# Revit family: PRD_AR_WshBsnWsts_RONDAWasteValve_ZANMW0030_0031
name_source: partatom
category: Plumbing Fixtures
revit_build: Autodesk Revit 2018 (Build: 20190510_1515(x64)
units: mm (PartAtom-declared; Revit-internal decimal feet)

## family parameters
Always vertical = No
Cut with Voids When Loaded = No
OmniClass Number = 23.45.00.00
OmniClass Title = Sanitary, Laundry, and Cleaning Equipment
Part Type = Normal
Room Calculation Point = No
Round Connector Dimension = Use Diameter
Shared = Yes
Work Plane-Based = Yes

## types (2) — shared parameters
AssetType = Fixed
Category = Pr_70_55_96_97, Washbasin wastes
Default Elevation = 1219 mm
DurationUnit = year
Features = chrome-plated brass, shaft valve and dome
Finish = chromed
GrossWeight = 0.34 kg
IfcExportAs = IfcWasteTerminalType
IfcExportType = WASTETRAP
IntegralAccessories = incl. an adapter for retrofitting on click closing dome
Manufacturer = KWC Group AG
ManufacturerName = KWC Group AG
ManufacturerURL = www.kwc.com
Material = brass
NBSDescription = Wastes for wash basins
NBSReference = 45-35-70/372
NetWeight = 0.32 kg
NominalDepth = 63 mm
NominalWidth = 63 mm
OutletConnectionSize = 32 mm
ProductInformation = https://pim.kwc.com
Quantity = 1
QuantityUom = Piece
Size = DN 32 (1 1/4 inch.)
TailorMade = No
URL = www.kwc.com
Uniclass2015Code = Pr_70_55_96_97
Uniclass2015Title = Washbasin wastes
Uniclass2015Version = Products v1.17
Version = 1
WarrantyDurationUnit = year
WasteValveMaterial = PRD_AR_ChromatedBrass
zero-valued in all types: InletConnectionSize, NominalHeight

## per-type parameters (varying)
| type | BIMObjectName | Color | Description | ModelNumber | Name | TopMaterial |
| ZANMW0030 | PRD_AR_WashbasinWastes_RONDAWasteValve_ZANMW0030 | chrome | Chrome-plated brass dome waste valve, shaft valve and dome, including an adapter for retrofitting on click closing dome, connection G 1 1/4 B | 2030057337 | Waste Valve ZANMW0030 | PRD_AR_ChromatedBrass |
| ZANMW0031 | PRD_AR_WashbasinWastes_RONDAWasteValve_ZANMW0031 | white | Chrome-plated brass dome waste valve, shaft valve, white (RAL 9003) powder-coated brass dome, including adapter for retrofitting on a click closing dome, connection G 1 1/4 B | 2030057339 | Waste Valve ZANMW0031 | PRD_AR_SyntheticWhite |

note: column(s) folded — value = type name in every type: Model, ModelReference

## geometry (parser evidence)
native form markers: Sweep x3
no freeform markers — native parametric forms only
